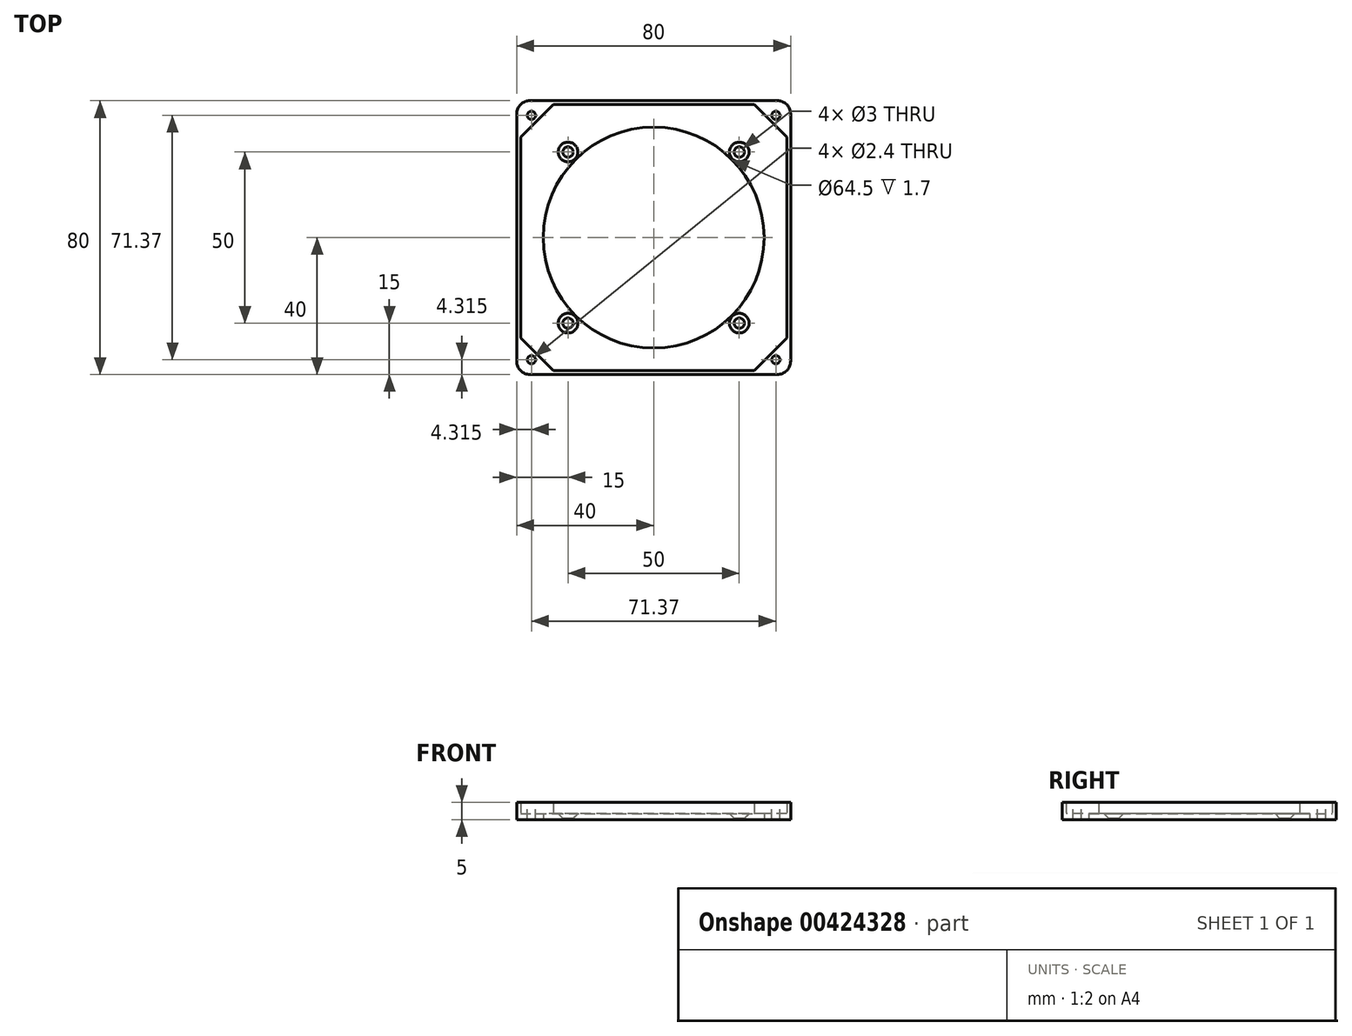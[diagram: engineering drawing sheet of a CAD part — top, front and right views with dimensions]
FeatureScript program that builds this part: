
annotation { "Feature Type Name" : "Feature", "Feature Type Description" : "" }
export const myFeature = defineFeature(function(context is Context, id is Id, definition is map)
    precondition{}
    {
        {
            var Q0;
            Q0=qCreatedBy(makeId("Top.planeOp"),FACE);
            var sketch = newSketch(context, id + "F0", { "sketchPlane" : qUnion([Q0])});
            skLineSegment(sketch, "E0.bottom", {"start": v(40, 40) * mm, "end": v(-40, 40) * mm});
            skLineSegment(sketch, "E0.top", {"start": v(40, -40) * mm, "end": v(-40, -40) * mm});
            skLineSegment(sketch, "E0.left", {"start": v(40, 40) * mm, "end": v(40, -40) * mm});
            skLineSegment(sketch, "E0.right", {"start": v(-40, 40) * mm, "end": v(-40, -40) * mm});
            skLineSegment(sketch, "E1.bottom", {"start": v(-38.86, 38.86) * mm, "end": v(38.86, 38.86) * mm});
            skLineSegment(sketch, "E1.top", {"start": v(-38.86, -38.86) * mm, "end": v(38.86, -38.86) * mm});
            skLineSegment(sketch, "E1.left", {"start": v(-38.86, 38.86) * mm, "end": v(-38.86, -38.86) * mm});
            skLineSegment(sketch, "E1.right", {"start": v(38.86, 38.86) * mm, "end": v(38.86, -38.86) * mm});
            skLineSegment(sketch, "E2", {"start": v(-38.86, 29.34) * mm, "end": v(-29.34, 38.86) * mm});
            skLineSegment(sketch, "E3", {"start": v(38.86, 29.34) * mm, "end": v(29.34, 38.86) * mm});
            skLineSegment(sketch, "E4", {"start": v(-38.86, -29.34) * mm, "end": v(-29.34, -38.86) * mm});
            skLineSegment(sketch, "E5", {"start": v(29.33, -38.86) * mm, "end": v(38.86, -29.34) * mm});
            skCircle(sketch, "E6", {"center": v(0, 0) * mm, "radius": 32.25 * mm});
            skSolve(sketch);
        }
        {
            var Q0;
            Q0=makeQuery(id+"F0.imprint","IMPRINT",FACE,{"disambiguationData":[TD([[makeQuery(id+"F0.imprint","IMPRINT",EDGE,{"derivedFrom":sQuery(id+"F0.wireOp",EDGE,"E0.bottom")}),1.0]])]});
            var Q1;
            {var subQ3=sQuery(id+"F0.wireOp",EDGE,"E2");Q1=makeQuery(id+"F0.imprint","IMPRINT",FACE,{"disambiguationData":[TD([[makeQuery(id+"F0.imprint","IMPRINT",EDGE,{"derivedFrom":subQ3}),1.0]])]});}
            var Q2;
            {var subQ3=sQuery(id+"F0.wireOp",EDGE,"E3");Q2=makeQuery(id+"F0.imprint","IMPRINT",FACE,{"disambiguationData":[TD([[makeQuery(id+"F0.imprint","IMPRINT",EDGE,{"derivedFrom":subQ3}),-1.0]])]});}
            var Q3;
            {var subQ3=sQuery(id+"F0.wireOp",EDGE,"E5");Q3=makeQuery(id+"F0.imprint","IMPRINT",FACE,{"disambiguationData":[TD([[makeQuery(id+"F0.imprint","IMPRINT",EDGE,{"derivedFrom":subQ3}),-1.0]])]});}
            var Q4;
            {var subQ3=sQuery(id+"F0.wireOp",EDGE,"E4");Q4=makeQuery(id+"F0.imprint","IMPRINT",FACE,{"disambiguationData":[TD([[makeQuery(id+"F0.imprint","IMPRINT",EDGE,{"derivedFrom":subQ3}),-1.0]])]});}
            extrude(context, id + "F1", {"entities" : qUnion([Q0, Q1, Q2, Q3, Q4]), "depth" : 5 * mm});
        }
        {
            var Q0;
            {var subQ3=sQuery(id+"F0.wireOp",EDGE,"E2");Q0=makeQuery(id+"F0.imprint","IMPRINT",FACE,{"disambiguationData":[TD([[makeQuery(id+"F0.imprint","IMPRINT",EDGE,{"derivedFrom":subQ3}),-1.0]])]});}
            extrude(context, id + "F2", {"entities" : qUnion([Q0]), "operationType" : NewBodyOperationType.ADD, "depth" : 1.7 * mm});
        }
        {
            var Q0;
            Q0=makeQuery(id+"F2.opExtrude","CAP_FACE",FACE,{"disambiguationData":[OSD([sQuery(id+"F0.wireOp",EDGE,"E1.bottom"),sQuery(id+"F0.wireOp",EDGE,"E1.left"),sQuery(id+"F0.wireOp",EDGE,"XLrHhnJ7-dGzd-Xrbb-NlTP-VvqNMSYbdhlf"),sQuery(id+"F0.wireOp",EDGE,"qSElXV0h-k4yD-cxAT-piWP-e7Eb2hw5FfI5")])],"isStart":false});
            var sketch = newSketch(context, id + "F3", { "sketchPlane" : qUnion([Q0])});
            skPoint(sketch, "E7", {"position": v(-25, 25) * mm});
            skPoint(sketch, "E8.0.1.0", {"position": v(-25, -25) * mm});
            skPoint(sketch, "E8.1.0.0", {"position": v(25, 25) * mm});
            skPoint(sketch, "E8.1.1.0", {"position": v(25, -25) * mm});
            skLineSegment(sketch, "E8.direction1", {"start": v(-25, 25) * mm, "end": v(25, 25) * mm, "construction": true});
            skLineSegment(sketch, "E8.direction2", {"start": v(-25, 25) * mm, "end": v(-25, -25) * mm, "construction": true});
            skSolve(sketch);
        }
        {
            var Q0;
            Q0=sQuery(id+"F3.wireOp",VERTEX,"E7");
            var Q1;
            Q1=sQuery(id+"F3.wireOp",VERTEX,"E8.1.0.0");
            var Q2;
            Q2=sQuery(id+"F3.wireOp",VERTEX,"E8.1.1.0");
            var Q3;
            Q3=sQuery(id+"F3.wireOp",VERTEX,"E8.0.1.0");
            var Q4;
            Q4=makeQuery(id+"F1.opExtrude","SWEPT_BODY",BODY,{"disambiguationData":[OSD([sQuery(id+"F0.wireOp",EDGE,"E0.bottom"),sQuery(id+"F0.wireOp",EDGE,"E0.top"),sQuery(id+"F0.wireOp",EDGE,"E0.left"),sQuery(id+"F0.wireOp",EDGE,"E0.right"),sQuery(id+"F0.wireOp",EDGE,"E1.bottom"),sQuery(id+"F0.wireOp",EDGE,"E1.top"),sQuery(id+"F0.wireOp",EDGE,"E1.left"),sQuery(id+"F0.wireOp",EDGE,"E1.right"),sQuery(id+"F0.wireOp",EDGE,"E2"),sQuery(id+"F0.wireOp",EDGE,"E3"),sQuery(id+"F0.wireOp",EDGE,"E4"),sQuery(id+"F0.wireOp",EDGE,"E5")])]});
            hole(context, id + "F4", {"style" : HoleStyle.C_SINK, "endStyle" : HoleEndStyle.THROUGH, "holeDiameter" : 3 * mm, "cSinkDiameter" : 5.75 * mm, "cSinkAngle" : 90 * degree, "isTappedThrough" : true, "tappedDepth" : 12 * mm, "tapClearance" : 3, "locations" : qUnion([Q0, Q1, Q2, Q3]), "scope" : qUnion([Q4])});
        }
        {
            var Q0;
            Q0=makeQuery(id+"F1.opExtrude","CAP_FACE",FACE,{"disambiguationData":[OSD([sQuery(id+"F0.wireOp",EDGE,"E0.bottom"),sQuery(id+"F0.wireOp",EDGE,"E0.top"),sQuery(id+"F0.wireOp",EDGE,"E0.left"),sQuery(id+"F0.wireOp",EDGE,"E0.right"),sQuery(id+"F0.wireOp",EDGE,"E1.bottom"),sQuery(id+"F0.wireOp",EDGE,"E1.top"),sQuery(id+"F0.wireOp",EDGE,"E1.left"),sQuery(id+"F0.wireOp",EDGE,"E1.right"),sQuery(id+"F0.wireOp",EDGE,"E2"),sQuery(id+"F0.wireOp",EDGE,"E3"),sQuery(id+"F0.wireOp",EDGE,"E4"),sQuery(id+"F0.wireOp",EDGE,"E5")])],"isStart":false});
            var sketch = newSketch(context, id + "F5", { "sketchPlane" : qUnion([Q0])});
            skPoint(sketch, "E9", {"position": v(-35.69, 35.69) * mm});
            skPoint(sketch, "E10.0.1.0", {"position": v(-35.69, -35.69) * mm});
            skPoint(sketch, "E10.1.0.0", {"position": v(35.68, 35.69) * mm});
            skPoint(sketch, "E10.1.1.0", {"position": v(35.68, -35.69) * mm});
            skLineSegment(sketch, "E10.direction1", {"start": v(-35.69, 35.69) * mm, "end": v(35.68, 35.69) * mm, "construction": true});
            skLineSegment(sketch, "E10.direction2", {"start": v(-35.69, 35.69) * mm, "end": v(-35.69, -35.69) * mm, "construction": true});
            skSolve(sketch);
        }
        {
            var Q0;
            Q0=sQuery(id+"F5.wireOp",VERTEX,"E9");
            var Q1;
            Q1=sQuery(id+"F5.wireOp",VERTEX,"E10.1.0.0");
            var Q2;
            Q2=sQuery(id+"F5.wireOp",VERTEX,"E10.1.1.0");
            var Q3;
            Q3=sQuery(id+"F5.wireOp",VERTEX,"E10.0.1.0");
            var Q4;
            Q4=makeQuery(id+"F1.opExtrude","SWEPT_BODY",BODY,{"disambiguationData":[OSD([sQuery(id+"F0.wireOp",EDGE,"E0.bottom"),sQuery(id+"F0.wireOp",EDGE,"E0.top"),sQuery(id+"F0.wireOp",EDGE,"E0.left"),sQuery(id+"F0.wireOp",EDGE,"E0.right"),sQuery(id+"F0.wireOp",EDGE,"E1.bottom"),sQuery(id+"F0.wireOp",EDGE,"E1.top"),sQuery(id+"F0.wireOp",EDGE,"E1.left"),sQuery(id+"F0.wireOp",EDGE,"E1.right"),sQuery(id+"F0.wireOp",EDGE,"E2"),sQuery(id+"F0.wireOp",EDGE,"E3"),sQuery(id+"F0.wireOp",EDGE,"E4"),sQuery(id+"F0.wireOp",EDGE,"E5")])]});
            hole(context, id + "F6", {"style" : HoleStyle.SIMPLE, "endStyle" : HoleEndStyle.THROUGH, "holeDiameter" : 2.4 * mm, "isTappedThrough" : true, "tappedDepth" : 12 * mm, "tapClearance" : 3, "locations" : qUnion([Q0, Q1, Q2, Q3]), "scope" : qUnion([Q4])});
        }
        {
            var Q0;
            Q0=makeQuery(id+"F1.opExtrude","SWEPT_EDGE",EDGE,{"disambiguationData":[OSD([sQuery(id+"F0.wireOp",EDGE,"E0.top"),sQuery(id+"F0.wireOp",EDGE,"E0.right")])]});
            var Q1;
            Q1=makeQuery(id+"F1.opExtrude","SWEPT_EDGE",EDGE,{"disambiguationData":[OSD([sQuery(id+"F0.wireOp",EDGE,"E0.top"),sQuery(id+"F0.wireOp",EDGE,"E0.left")])]});
            var Q2;
            Q2=makeQuery(id+"F1.opExtrude","SWEPT_EDGE",EDGE,{"disambiguationData":[OSD([sQuery(id+"F0.wireOp",EDGE,"E0.bottom"),sQuery(id+"F0.wireOp",EDGE,"E0.left")])]});
            var Q3;
            Q3=makeQuery(id+"F1.opExtrude","SWEPT_EDGE",EDGE,{"disambiguationData":[OSD([sQuery(id+"F0.wireOp",EDGE,"E0.bottom"),sQuery(id+"F0.wireOp",EDGE,"E0.right")])]});
            fillet(context, id + "F7", {"entities" : qUnion([Q0, Q1, Q2, Q3]), "radius" : 3.9 * mm, "tangentPropagation" : true, "allowEdgeOverflow" : false});
        }
    });
